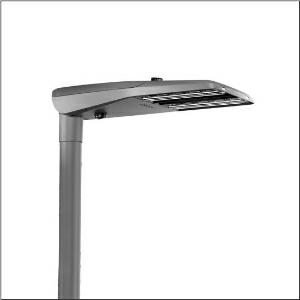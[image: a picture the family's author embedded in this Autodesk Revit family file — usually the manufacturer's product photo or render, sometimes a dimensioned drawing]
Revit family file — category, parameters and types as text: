
# Revit family: streetlight_sl_11_iq_midi___st1_2a_5xc3a61y08me_9d9d
name_source: partatom
category: Lighting Fixtures
units: mm (PartAtom-declared; Revit-internal decimal feet)

## family parameters
Cut with Voids When Loaded = No
Host = Face
Light Source = No
Part Type = Normal
Room Calculation Point = No
Round Connector Dimension = Use Diameter
Shared = No

## types (1)
- --- (1 x LED, 16240 lm, 122.7 W, 2700K)
    Apparent Load = 123 VA
    CIE Flux Codes = 32 70 96 100 100
    Color Rendering = 70
    Color Temperature = 2700K
    Default Elevation = 1800 mm
    Description = Streetlight SL 11 iQ midi, mast luminaire, primary light control with 3 zone facetted reflector, of plastic, silver coated, highly specular, primary optical cover: cover, of PMMA, transparent, light distribution: ST1.2a, light emission: direct distribution, primary light characteristic: asymmetric, installation type: post-top, side-entry, lamps: LED, High Power LED, rated values: 16.240lm | 122,7W | 132,4lm/W (begin service life); end service life: 16.240lm | 130,2W; at 50% lumin. flux: 8.120lm | 56,1W | 144,7lm/W, colour temperature: 2700K, colour rendering: CRI > 70, light colour: 727, light setting 1 begin service life: 100% | 16.240lm | 122,7W | 132,4lm/W | 2.700K, light setting 1 end service life: 130,2W, further light settings possible, control: pre-setting: logarithmic dimming characteristic, Street-Remote, Auto-Match, Temp-Guard, Lumen-Switch, Night-Set, Smart-Wire, Light-Fading, Desk-Remote (wireless, voltage-free reading and setting of iQ features in the workshop via application-optimized NFC function/RFID function), optimised constant luminous flux control (CLO 2.0), with cable H07RN-F 5x 1.5mm², mains connection: 230..240V, AC, 50/60Hz, connection cable pre-assembled, cable length: 12,5m, luminaire housing, of diecast aluminium, powder-coated, Siteco® metallic grey (DB 702S), please order mast flange separately, inclination adjustable without tools: 0°, 5°, 10°, 15° (post-top) | 0°, -5°, -10°, -15° (side-entry), sealing non-destructively replaceable, multi-level sealing system, length: 780mm, width: 376mm, height: 118mm, mast flange for spigot size: 42mm (side-entry): 5XC10008XM4, 60/48mm (side-entry/post-top): 5XC10108XM2, 76/60mm (side-entry/post-top): 5XC10108XM1, equipment: Power, Smart Interface below and above, protection rating (complete): IP66, insulation class (complete): insulation class II (safety insulation), certification: CE, ENEC, ENEC+, VDE, UKCA, impact resistance: IK10, permissible operating ambient temperature for outdoor applications: -25..+50°C, standard-compliant lighting for roads and squares, Environmental Product Declaration (EPD) tested and certified by an independent institute, packaging unit: 1 piece

Light Distribution: ST1.2a
    Height = 118 mm
    Lamp = 1 x LED
    Lamp Light Flux = 16240 lm
    Lamp Power = 122.7 W
    Lamp count = 1
    Length = 780 mm
    Luminous efficacy = 132 lm/W
    Manufacturer = Siteco
    ModVariant = No
    Model = 5XC3A61Y08ME
    Number of Poles = 1
    OnlyDefault = Yes
    Power Factor = 1
    Product Name = Streetlight SL 11 iQ midi | ST1.2a
    Product group = mast luminaire | pylon top
    ProductGroupID = 6100
    Protection Class = Protection class II
    Protection Degree = IP 66
    RLX_Detail_Level = 1
    RLX_Emergency_Light_Flux = 0 lm
    RLX_Emergency_Type = 0
    RLX_Emergency_Type_DB = No
    RlxData = <blob elided: 69953 chars, md5=f08ebbea>
    Socket = socket
    Standby Power = 0 W
    System Light Flux = 16241 lm
    System Power = 123 W
    Type Comments = factory setting: luminous flux: 100 % | dim-lin: 254 | 553 mA
    Type Image = l_1004429.jpg
    URL = http://relux.com
    VarID = @adj_154517
    Voltage = 0 V
    Weight = 0.00 kg
    Width = 376 mm

## geometry (parser evidence)
native form markers: Blend x4, Sweep x9
no freeform markers — native parametric forms only
